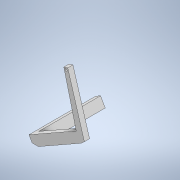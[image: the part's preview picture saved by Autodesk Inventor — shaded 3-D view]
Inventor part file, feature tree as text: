
AUTODESK INVENTOR PART (.ipt)
format: ipt  version: 2021 (Build 250183000, 183)  size: 142,848 bytes
history: native  units: mm
features: extrude x3, sketch x3
ambient origin geometry x8: Origin, YZ Plane, XZ Plane, XY Plane, X Axis, Y Axis, Z Axis, Center Point
bodies: Solid1 (feature_tree)
feature tree (6):
  extrude  "Extrusion1"  Depth=5.165078mm
  extrude  "Extrusion2"  Depth=120.895449mm
  extrude  "Extrusion3"  Depth=274.0mm
  sketch  "Sketch1"  dims[d1=10.542886mm d2=5.165078mm]
  sketch  "Sketch2"  dims[d10=233.093698mm d11=120.895449mm]
  sketch  "Sketch3"  dims[d12=24.243525mm d13=13.768721mm d14=196.983667mm d15=220.055283mm d16=159.179802mm d17=152.002472mm d18=356.005789mm d19=23.0mm d20=0.0mm d21=274.0mm d22=0.0mm d23=63.016mm d24=0.693mm d25=274.0mm d26=0.0mm]
